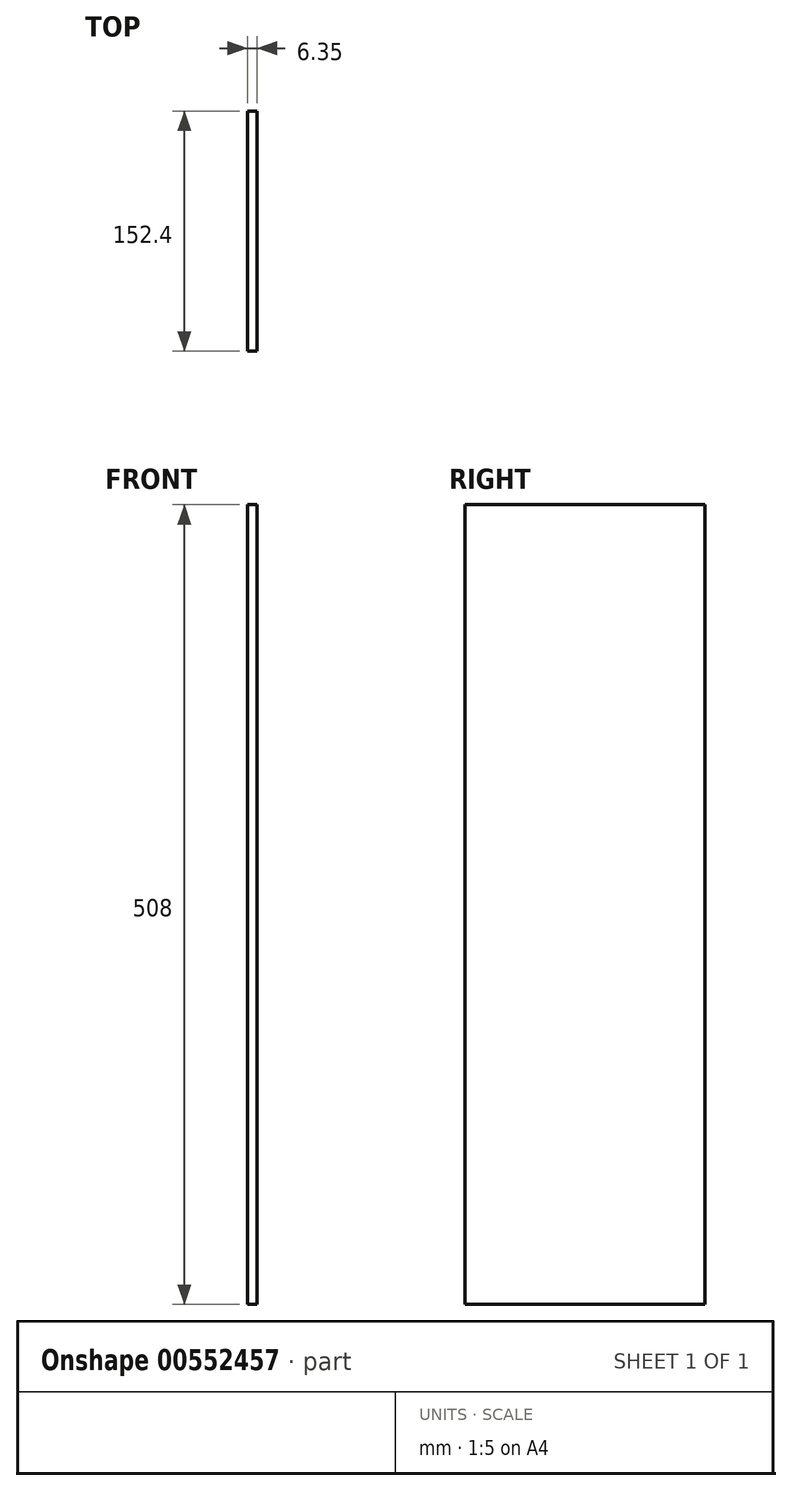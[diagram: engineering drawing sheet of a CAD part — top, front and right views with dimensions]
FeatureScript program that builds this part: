
annotation { "Feature Type Name" : "Feature", "Feature Type Description" : "" }
export const myFeature = defineFeature(function(context is Context, id is Id, definition is map)
    precondition{}
    {
        {
            var Q0;
            Q0=qCreatedBy(makeId("Front.planeOp"),FACE);
            var sketch = newSketch(context, id + "F0", { "sketchPlane" : qUnion([Q0])});
            skLineSegment(sketch, "E0.bottom", {"start": v(0, 0) * mm, "end": v(6.35, 0) * mm});
            skLineSegment(sketch, "E0.top", {"start": v(0, 508) * mm, "end": v(6.35, 508) * mm});
            skLineSegment(sketch, "E0.left", {"start": v(0, 0) * mm, "end": v(0, 508) * mm});
            skLineSegment(sketch, "E0.right", {"start": v(6.35, 0) * mm, "end": v(6.35, 508) * mm});
            skSolve(sketch);
        }
        {
            var Q0;
            Q0 = qSketchRegion(id + "F0", true);
            extrude(context, id + "F1", {"entities" : qUnion([Q0]), "depth" : 152.4 * mm, "offsetDistance" : 25.4 * mm});
        }
    });
